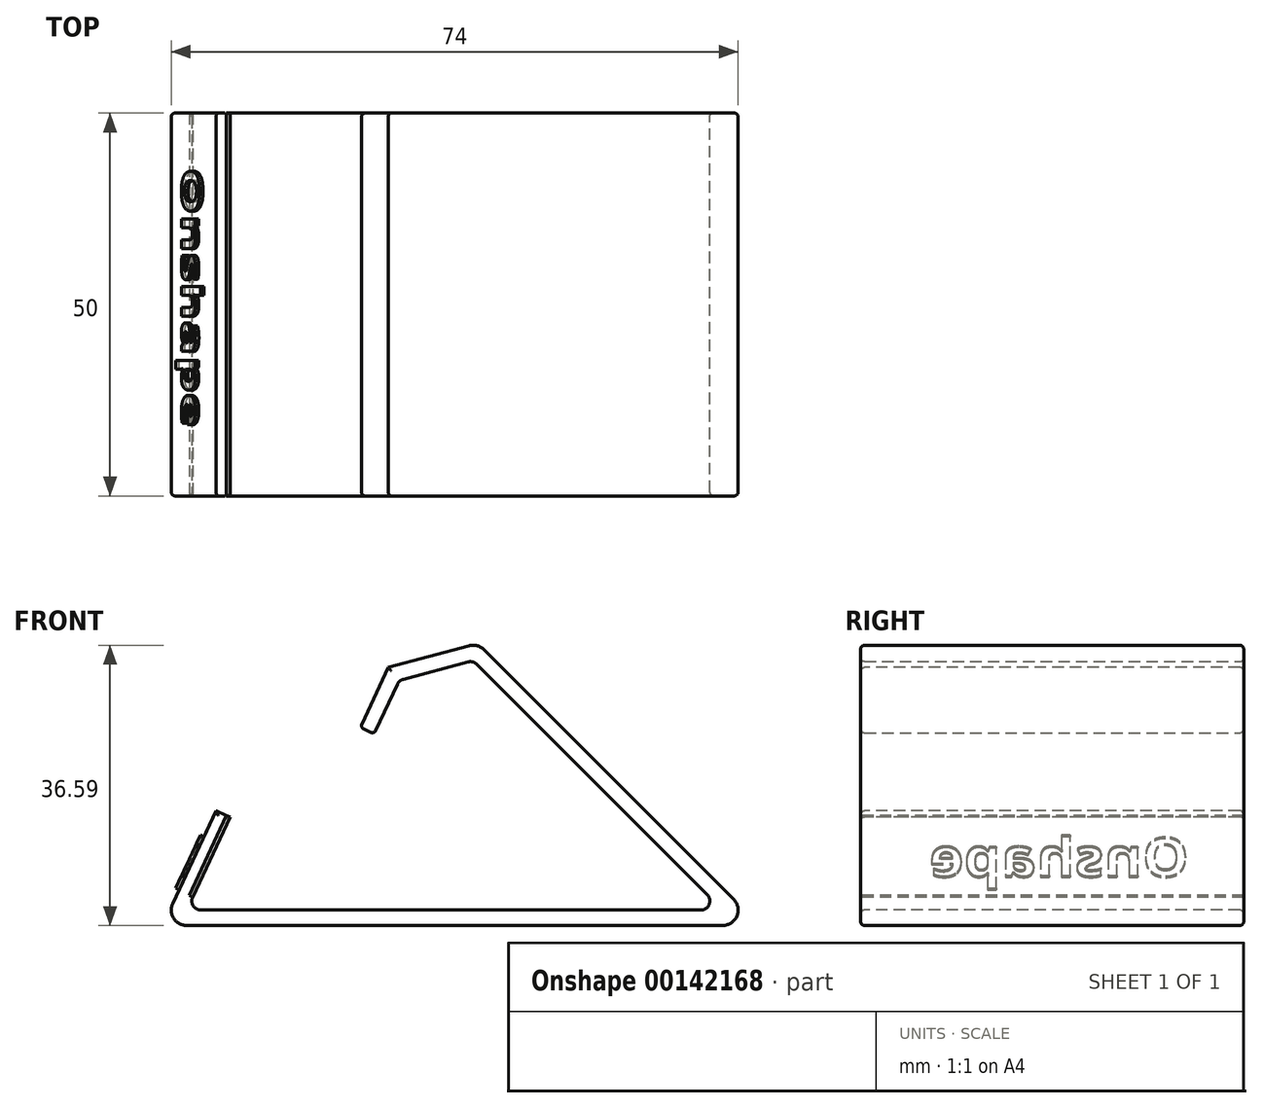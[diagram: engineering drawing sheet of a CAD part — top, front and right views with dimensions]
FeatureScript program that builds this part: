
annotation { "Feature Type Name" : "Feature", "Feature Type Description" : "" }
export const myFeature = defineFeature(function(context is Context, id is Id, definition is map)
    precondition{}
    {
        {
            var Q0;
            Q0=qCreatedBy(makeId("Front.planeOp"),FACE);
            var sketch = newSketch(context, id + "F0", { "sketchPlane" : qUnion([Q0])});
            skLineSegment(sketch, "E0", {"start": v(0, 0) * mm, "end": v(70, 0) * mm});
            skLineSegment(sketch, "E1", {"start": v(70, 0) * mm, "end": v(37.41, 32.59) * mm});
            skLineSegment(sketch, "E2", {"start": v(37.41, 32.59) * mm, "end": v(27.75, 30) * mm});
            skLineSegment(sketch, "E3", {"start": v(27.75, 30) * mm, "end": v(24.49, 23) * mm});
            skLineSegment(sketch, "E4", {"start": v(0, 0) * mm, "end": v(5.67, 12.15) * mm});
            skLineSegment(sketch, "E5.0", {"start": v(26.33, 31.7) * mm, "end": v(22.68, 23.85) * mm});
            skLineSegment(sketch, "E5.1", {"start": v(38, 34.82) * mm, "end": v(26.33, 31.7) * mm});
            skLineSegment(sketch, "E5.2", {"start": v(74.83, -2) * mm, "end": v(38, 34.82) * mm});
            skLineSegment(sketch, "E5.3", {"start": v(-3.14, -2) * mm, "end": v(74.83, -2) * mm});
            skLineSegment(sketch, "E6.0", {"start": v(-3.14, -2) * mm, "end": v(3.86, 13) * mm});
            skLineSegment(sketch, "E7", {"start": v(3.86, 13) * mm, "end": v(5.67, 12.15) * mm});
            skLineSegment(sketch, "E8", {"start": v(22.68, 23.85) * mm, "end": v(24.49, 23) * mm});
            skSolve(sketch);
        }
        {
            var Q0;
            Q0 = qSketchRegion(id + "F0", true);
            extrude(context, id + "F1", {"entities" : qUnion([Q0]), "oppositeDirection" : true, "depth" : 50 * mm});
        }
        {
            var Q0;
            Q0=makeQuery(id+"F1.opExtrude","SWEPT_EDGE",EDGE,{"disambiguationData":[OSD([sQuery(id+"F0.wireOp",EDGE,"E5.1"),sQuery(id+"F0.wireOp",EDGE,"E5.2")])]});
            var Q1;
            Q1=makeQuery(id+"F1.opExtrude","SWEPT_EDGE",EDGE,{"disambiguationData":[OSD([sQuery(id+"F0.wireOp",EDGE,"E5.2"),sQuery(id+"F0.wireOp",EDGE,"E5.3")])]});
            var Q2;
            Q2=makeQuery(id+"F1.opExtrude","SWEPT_EDGE",EDGE,{"disambiguationData":[OSD([sQuery(id+"F0.wireOp",EDGE,"E5.3"),sQuery(id+"F0.wireOp",EDGE,"E6.0")])]});
            fillet(context, id + "F2", {"entities" : qUnion([Q0, Q1, Q2]), "radius" : 2 * mm, "tangentPropagation" : true, "allowEdgeOverflow" : false});
        }
        {
            var Q0;
            Q0=makeQuery(id+"F1.opExtrude","SWEPT_FACE",FACE,{"disambiguationData":[OSD([sQuery(id+"F0.wireOp",EDGE,"E6.0")])]});
            var sketch = newSketch(context, id + "F3", { "sketchPlane" : qUnion([Q0])});
            skText(sketch, "E9", { "text": "Onshape", "fontName": "OpenSans-Bold.ttf"});
            const initialGuessF3  = {"E9": [-0.04284, 0.00382, 1, 0, 0.0055]};
            skSetInitialGuess(sketch, initialGuessF3);
            skSolve(sketch);
        }
        {
            var Q0;
            Q0=makeQuery(id+"F1.opExtrude","SWEPT_EDGE",EDGE,{"disambiguationData":[OSD([sQuery(id+"F0.wireOp",EDGE,"E0"),sQuery(id+"F0.wireOp",EDGE,"E1")])]});
            var Q1;
            Q1=makeQuery(id+"F1.opExtrude","SWEPT_EDGE",EDGE,{"disambiguationData":[OSD([sQuery(id+"F0.wireOp",EDGE,"E1"),sQuery(id+"F0.wireOp",EDGE,"E2")])]});
            var Q2;
            Q2=makeQuery(id+"F1.opExtrude","SWEPT_EDGE",EDGE,{"disambiguationData":[OSD([sQuery(id+"F0.wireOp",EDGE,"E2"),sQuery(id+"F0.wireOp",EDGE,"E3")])]});
            var Q3;
            Q3=makeQuery(id+"F1.opExtrude","SWEPT_EDGE",EDGE,{"disambiguationData":[OSD([sQuery(id+"F0.wireOp",EDGE,"E0"),sQuery(id+"F0.wireOp",EDGE,"E4")])]});
            fillet(context, id + "F4", {"entities" : qUnion([Q0, Q1, Q2, Q3]), "radius" : 1.2 * mm, "tangentPropagation" : true, "allowEdgeOverflow" : false});
        }
        {
            var Q0;
            Q0 = qSketchRegion(id + "F3", true);
            var Q1;
            Q1=makeQuery(id+"F1.opExtrude","SWEPT_FACE",FACE,{"disambiguationData":[OSD([sQuery(id+"F0.wireOp",EDGE,"E4")])]});
            extrude(context, id + "F5", {"entities" : qUnion([Q0, Q1]), "depth" : 0.5 * mm});
        }
        {
            var Q0;
            Q0=makeQuery(id+"F1.opExtrude","SWEPT_FACE",FACE,{"disambiguationData":[OSD([sQuery(id+"F0.wireOp",EDGE,"E7")])]});
            var Q1;
            Q1=makeQuery(id+"F1.opExtrude","CAP_FACE",FACE,{"disambiguationData":[OSD([sQuery(id+"F0.wireOp",EDGE,"E0"),sQuery(id+"F0.wireOp",EDGE,"E1"),sQuery(id+"F0.wireOp",EDGE,"E2"),sQuery(id+"F0.wireOp",EDGE,"E3"),sQuery(id+"F0.wireOp",EDGE,"E4"),sQuery(id+"F0.wireOp",EDGE,"E5.0"),sQuery(id+"F0.wireOp",EDGE,"E5.1"),sQuery(id+"F0.wireOp",EDGE,"E5.2"),sQuery(id+"F0.wireOp",EDGE,"E5.3"),sQuery(id+"F0.wireOp",EDGE,"E6.0"),sQuery(id+"F0.wireOp",EDGE,"E7"),sQuery(id+"F0.wireOp",EDGE,"E8")])],"isStart":false});
            var Q2;
            Q2=makeQuery(id+"F1.opExtrude","SWEPT_FACE",FACE,{"disambiguationData":[OSD([sQuery(id+"F0.wireOp",EDGE,"E8")])]});
            var Q3;
            Q3=makeQuery(id+"F1.opExtrude","CAP_FACE",FACE,{"disambiguationData":[OSD([sQuery(id+"F0.wireOp",EDGE,"E0"),sQuery(id+"F0.wireOp",EDGE,"E1"),sQuery(id+"F0.wireOp",EDGE,"E2"),sQuery(id+"F0.wireOp",EDGE,"E3"),sQuery(id+"F0.wireOp",EDGE,"E4"),sQuery(id+"F0.wireOp",EDGE,"E5.0"),sQuery(id+"F0.wireOp",EDGE,"E5.1"),sQuery(id+"F0.wireOp",EDGE,"E5.2"),sQuery(id+"F0.wireOp",EDGE,"E5.3"),sQuery(id+"F0.wireOp",EDGE,"E6.0"),sQuery(id+"F0.wireOp",EDGE,"E7"),sQuery(id+"F0.wireOp",EDGE,"E8")])],"isStart":true});
            fillet(context, id + "F6", {"entities" : qUnion([Q0, Q1, Q2, Q3]), "radius" : 0.5 * mm, "tangentPropagation" : true, "allowEdgeOverflow" : false});
        }
    });
